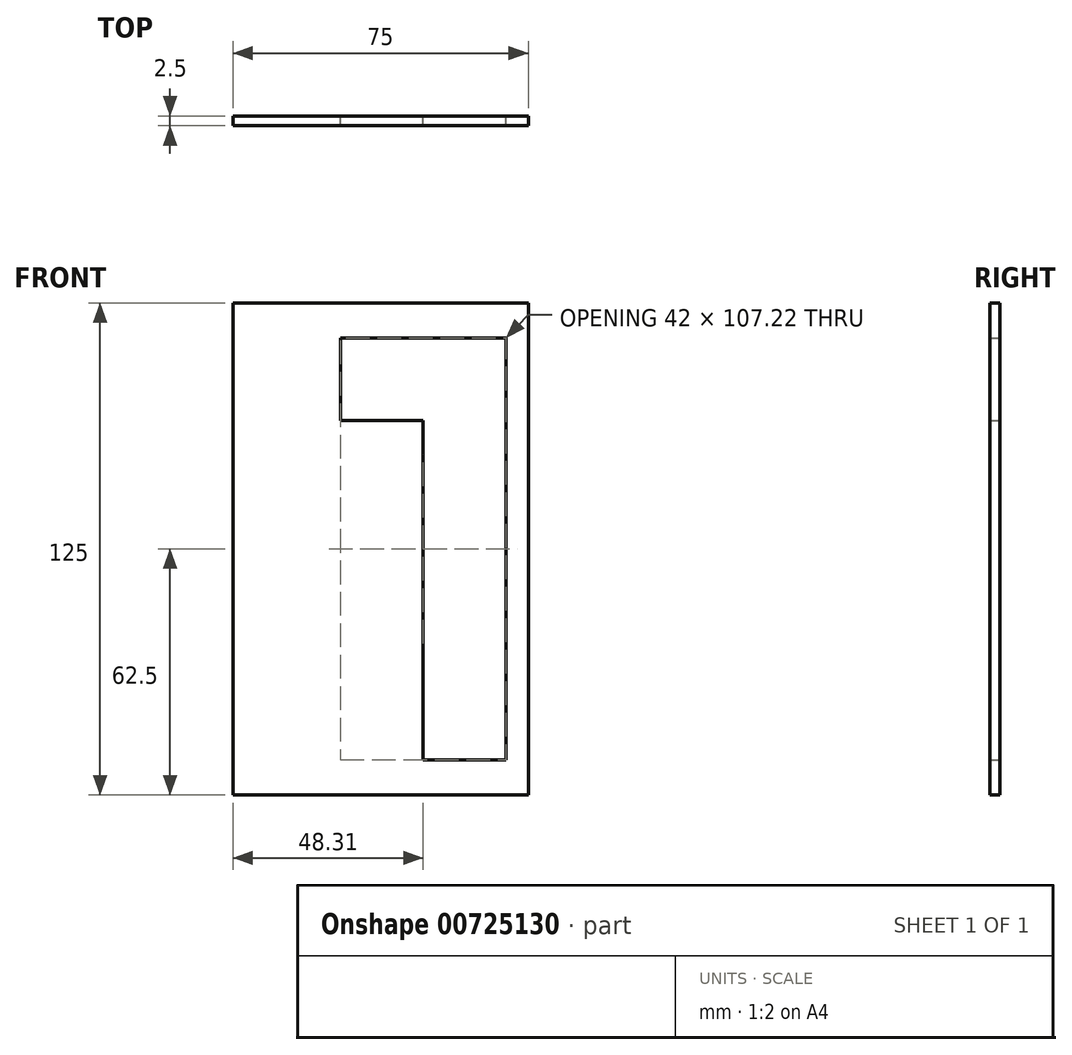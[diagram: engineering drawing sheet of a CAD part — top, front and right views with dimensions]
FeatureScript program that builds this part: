
annotation { "Feature Type Name" : "Feature", "Feature Type Description" : "" }
export const myFeature = defineFeature(function(context is Context, id is Id, definition is map)
    precondition{}
    {
        {
            var Q0;
            Q0=qCreatedBy(makeId("Front.planeOp"),FACE);
            var sketch = newSketch(context, id + "F0", { "sketchPlane" : qUnion([Q0])});
            skLineSegment(sketch, "E0.bottom", {"start": v(0, 0) * mm, "end": v(75, 0) * mm});
            skLineSegment(sketch, "E0.left", {"start": v(0, 0) * mm, "end": v(0, 125) * mm});
            skLineSegment(sketch, "E1.top", {"start": v(3.8, 3.81) * mm, "end": v(71.19, 3.81) * mm});
            skLineSegment(sketch, "E1.left", {"start": v(3.8, 121.19) * mm, "end": v(3.8, 3.8) * mm});
            skLineSegment(sketch, "E2.bottom", {"start": v(0, 125) * mm, "end": v(44.5, 125) * mm});
            skLineSegment(sketch, "E2.top", {"start": v(0, 125) * mm, "end": v(44.5, 125) * mm});
            skLineSegment(sketch, "E2.left", {"start": v(-9.85, 63.52) * mm, "end": v(-9.85, 63.52) * mm});
            skLineSegment(sketch, "E3", {"start": v(3.8, 121.19) * mm, "end": v(44.5, 121.19) * mm});
            skLineSegment(sketch, "E4", {"start": v(50.19, 121.19) * mm, "end": v(50.19, 125) * mm});
            skLineSegment(sketch, "E5", {"start": v(44.5, 125) * mm, "end": v(50.19, 125) * mm});
            skLineSegment(sketch, "E6", {"start": v(50.19, 121.19) * mm, "end": v(44.5, 121.19) * mm});
            skLineSegment(sketch, "E7", {"start": v(71.19, 3.81) * mm, "end": v(71.19, 125) * mm});
            skLineSegment(sketch, "E8", {"start": v(71.19, 125) * mm, "end": v(75, 125) * mm});
            skLineSegment(sketch, "E9", {"start": v(75, 125) * mm, "end": v(75, 0) * mm});
            skLineSegment(sketch, "E10", {"start": v(50.19, 121.19) * mm, "end": v(71.19, 121.19) * mm});
            skLineSegment(sketch, "E11", {"start": v(50.19, 125) * mm, "end": v(71.19, 125) * mm});
            skLineSegment(sketch, "E12", {"start": v(8.89, 8.9) * mm, "end": v(8.89, 29.9) * mm});
            skLineSegment(sketch, "E13", {"start": v(8.89, 29.89) * mm, "end": v(19.05, 29.9) * mm});
            skLineSegment(sketch, "E14", {"start": v(19.05, 29.89) * mm, "end": v(19.05, 68.82) * mm});
            skLineSegment(sketch, "E15", {"start": v(19.05, 68.82) * mm, "end": v(8.89, 68.82) * mm});
            skLineSegment(sketch, "E16", {"start": v(8.89, 68.82) * mm, "end": v(8.89, 116.11) * mm});
            skLineSegment(sketch, "E17", {"start": v(8.89, 116.11) * mm, "end": v(69.3, 116.11) * mm});
            skLineSegment(sketch, "E18", {"start": v(69.3, 116.11) * mm, "end": v(69.3, 8.9) * mm});
            skLineSegment(sketch, "E19", {"start": v(69.3, 8.9) * mm, "end": v(48.3, 8.9) * mm});
            skLineSegment(sketch, "E20", {"start": v(48.3, 8.9) * mm, "end": v(48.3, 95.11) * mm});
            skLineSegment(sketch, "E21", {"start": v(48.3, 95.11) * mm, "end": v(27.3, 95.11) * mm});
            skLineSegment(sketch, "E22", {"start": v(27.3, 95.11) * mm, "end": v(27.3, 89.82) * mm});
            skLineSegment(sketch, "E23", {"start": v(27.3, 89.82) * mm, "end": v(40.05, 89.82) * mm});
            skLineSegment(sketch, "E24", {"start": v(40.05, 89.82) * mm, "end": v(40.05, 8.9) * mm});
            skLineSegment(sketch, "E25", {"start": v(40.05, 8.9) * mm, "end": v(8.89, 8.9) * mm});
            skLineSegment(sketch, "E26", {"start": v(27.3, 95.11) * mm, "end": v(27.3, 116.11) * mm});
            skSolve(sketch);
        }
        {
            var Q0;
            Q0 = qSketchRegion(id + "F0", true);
            var Q1;
            {var subQ1=sQuery(id+"F0.wireOp",EDGE,"E1.top");Q1=makeQuery(id+"F0.imprint","IMPRINT",FACE,{"disambiguationData":[TD([[makeQuery(id+"F0.imprint","IMPRINT",EDGE,{"derivedFrom":subQ1}),1.0]])]});}
            var Q2;
            Q2=makeQuery(id+"F0.imprint","IMPRINT",FACE,{"disambiguationData":[TD([[makeQuery(id+"F0.imprint","IMPRINT",EDGE,{"derivedFrom":sQuery(id+"F0.wireOp",EDGE,"E12")}),-1.0]])]});
            extrude(context, id + "F1", {"entities" : qUnion([Q0, Q1, Q2]), "depth" : 2.5 * mm, "offsetDistance" : 25.4 * mm});
        }
    });
